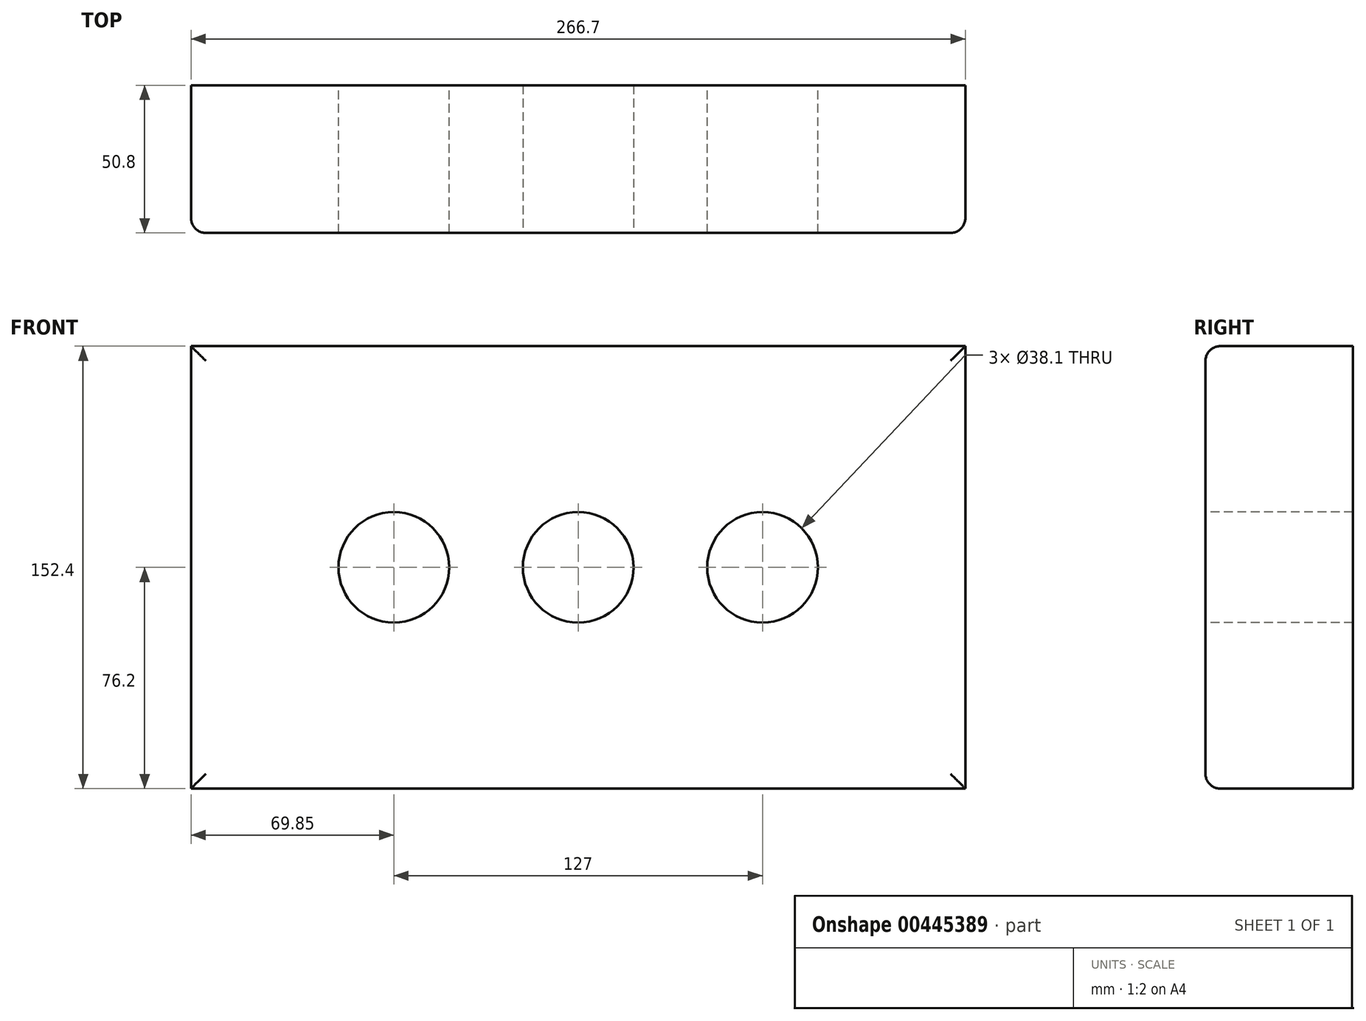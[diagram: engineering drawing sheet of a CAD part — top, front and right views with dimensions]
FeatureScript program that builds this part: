
annotation { "Feature Type Name" : "Feature", "Feature Type Description" : "" }
export const myFeature = defineFeature(function(context is Context, id is Id, definition is map)
    precondition{}
    {
        {
            var Q0;
            Q0=qCreatedBy(makeId("Front.planeOp"),FACE);
            var sketch = newSketch(context, id + "F0", { "sketchPlane" : qUnion([Q0])});
            skLineSegment(sketch, "E0.bottom", {"start": v(133.35, 76.2) * mm, "end": v(-133.35, 76.2) * mm});
            skLineSegment(sketch, "E0.top", {"start": v(133.35, -76.2) * mm, "end": v(-133.35, -76.2) * mm});
            skLineSegment(sketch, "E0.left", {"start": v(133.35, 76.2) * mm, "end": v(133.35, -76.2) * mm});
            skLineSegment(sketch, "E0.right", {"start": v(-133.35, 76.2) * mm, "end": v(-133.35, -76.2) * mm});
            skPoint(sketch, "E0.middle", {"position": v(0, 0) * mm});
            skSolve(sketch);
        }
        {
            var Q0;
            Q0=makeQuery(id+"F0.imprint","IMPRINT",FACE,{"disambiguationData":[TD([[makeQuery(id+"F0.imprint","IMPRINT",EDGE,{"derivedFrom":sQuery(id+"F0.wireOp",EDGE,"E0.bottom")}),1.0]])]});
            extrude(context, id + "F1", {"entities" : qUnion([Q0]), "depth" : 50.8 * mm});
        }
        {
            var Q0;
            Q0=makeQuery(id+"F1.opExtrude","CAP_FACE",FACE,{"disambiguationData":[OSD([sQuery(id+"F0.wireOp",EDGE,"E0.bottom"),sQuery(id+"F0.wireOp",EDGE,"E0.top"),sQuery(id+"F0.wireOp",EDGE,"E0.left"),sQuery(id+"F0.wireOp",EDGE,"E0.right")])],"isStart":false});
            var sketch = newSketch(context, id + "F2", { "sketchPlane" : qUnion([Q0])});
            skCircle(sketch, "E1", {"center": v(0, 0) * mm, "radius": 19.05 * mm});
            skSolve(sketch);
        }
        {
            var Q0;
            Q0=makeQuery(id+"F2.imprint","IMPRINT",FACE,{"disambiguationData":[TD([[makeQuery(id+"F2.imprint","IMPRINT",EDGE,{"derivedFrom":sQuery(id+"F2.wireOp",EDGE,"E1")}),1.0]])]});
            extrude(context, id + "F3", {"entities" : qUnion([Q0]), "operationType" : NewBodyOperationType.REMOVE, "oppositeDirection" : true, "depth" : 76.2 * mm});
        }
        {
            var Q0;
            Q0=qCreatedBy(makeId("Front.planeOp"),FACE);
            var sketch = newSketch(context, id + "F4", { "sketchPlane" : qUnion([Q0])});
            skCircle(sketch, "E2", {"center": v(-63.5, 0) * mm, "radius": 19.05 * mm});
            skSolve(sketch);
        }
        {
            var Q0;
            Q0=makeQuery(id+"F4.imprint","IMPRINT",FACE,{"disambiguationData":[TD([[makeQuery(id+"F4.imprint","IMPRINT",EDGE,{"derivedFrom":sQuery(id+"F4.wireOp",EDGE,"E2")}),1.0]])]});
            extrude(context, id + "F5", {"entities" : qUnion([Q0]), "operationType" : NewBodyOperationType.REMOVE, "depth" : 50.8 * mm});
        }
        {
            var Q0;
            Q0=qCreatedBy(makeId("Front.planeOp"),FACE);
            var sketch = newSketch(context, id + "F6", { "sketchPlane" : qUnion([Q0])});
            skCircle(sketch, "E3", {"center": v(63.5, 0) * mm, "radius": 19.05 * mm});
            skSolve(sketch);
        }
        {
            var Q0;
            Q0=makeQuery(id+"F6.imprint","IMPRINT",FACE,{"disambiguationData":[TD([[makeQuery(id+"F6.imprint","IMPRINT",EDGE,{"derivedFrom":sQuery(id+"F6.wireOp",EDGE,"E3")}),1.0]])]});
            extrude(context, id + "F7", {"entities" : qUnion([Q0]), "operationType" : NewBodyOperationType.REMOVE, "depth" : 50.8 * mm});
        }
        {
            var Q0;
            Q0=makeQuery(id+"F1.opExtrude","CAP_EDGE",EDGE,{"disambiguationData":[OSD([sQuery(id+"F0.wireOp",EDGE,"E0.bottom")])],"isStart":false});
            var Q1;
            Q1=makeQuery(id+"F1.opExtrude","CAP_EDGE",EDGE,{"disambiguationData":[OSD([sQuery(id+"F0.wireOp",EDGE,"E0.right")])],"isStart":false});
            var Q2;
            Q2=makeQuery(id+"F1.opExtrude","CAP_EDGE",EDGE,{"disambiguationData":[OSD([sQuery(id+"F0.wireOp",EDGE,"E0.top")])],"isStart":false});
            var Q3;
            Q3=makeQuery(id+"F1.opExtrude","CAP_EDGE",EDGE,{"disambiguationData":[OSD([sQuery(id+"F0.wireOp",EDGE,"E0.left")])],"isStart":false});
            fillet(context, id + "F8", {"entities" : qUnion([Q0, Q1, Q2, Q3]), "radius" : 5.08 * mm, "tangentPropagation" : true, "allowEdgeOverflow" : false});
        }
    });
